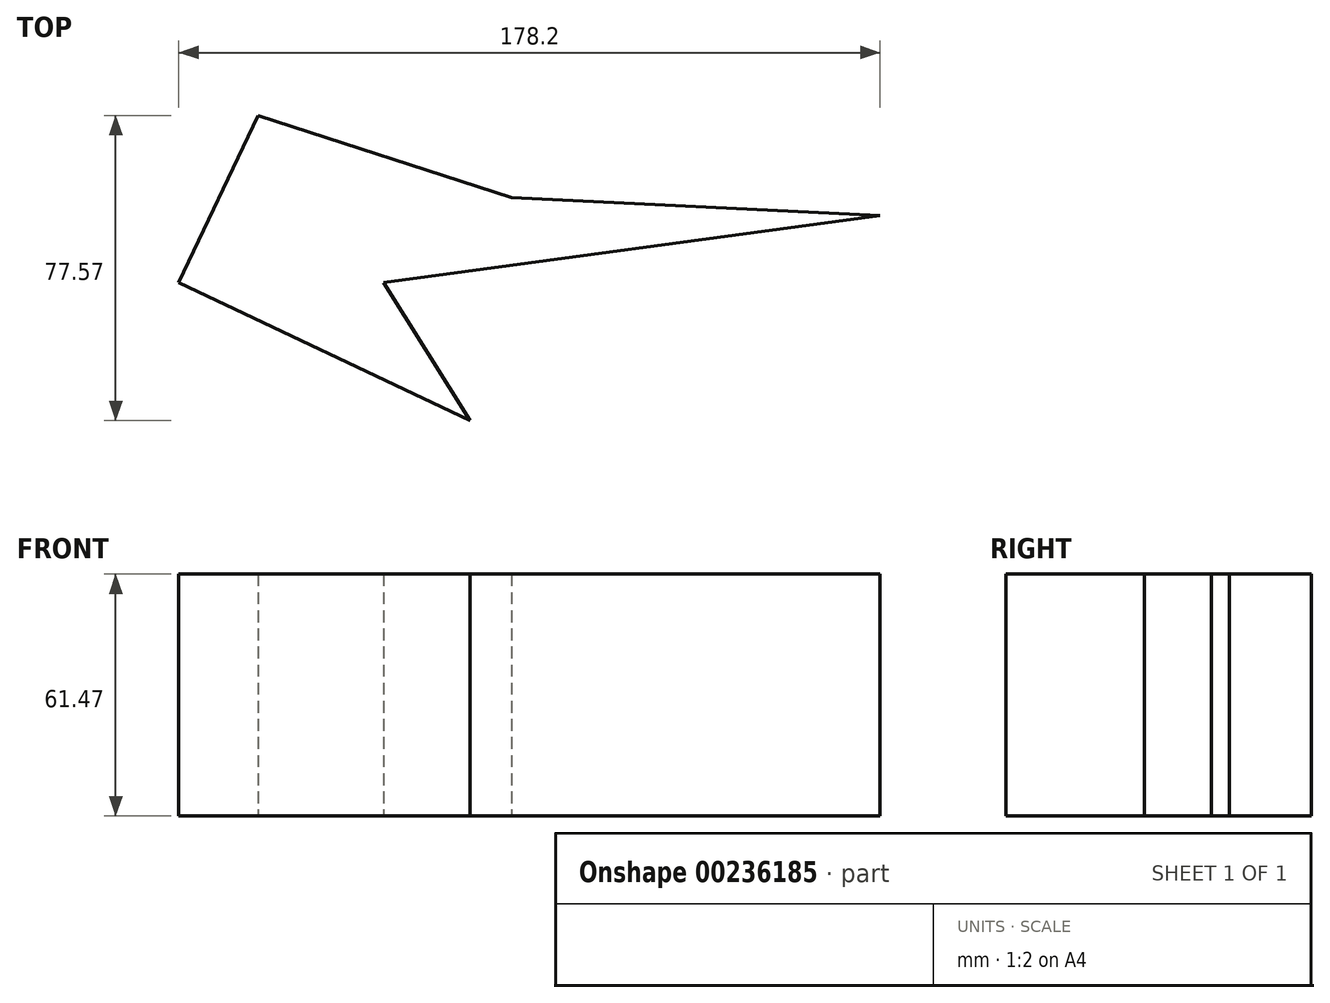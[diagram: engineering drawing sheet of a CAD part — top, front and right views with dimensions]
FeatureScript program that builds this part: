
annotation { "Feature Type Name" : "Feature", "Feature Type Description" : "" }
export const myFeature = defineFeature(function(context is Context, id is Id, definition is map)
    precondition{}
    {
        {
            var Q0;
            Q0=qCreatedBy(makeId("Top.planeOp"),FACE);
            var sketch = newSketch(context, id + "F0", { "sketchPlane" : qUnion([Q0])});
            skLineSegment(sketch, "E0", {"start": v(44.55, 16.26) * mm, "end": v(-19.8, 37.13) * mm});
            skLineSegment(sketch, "E1", {"start": v(-19.8, 37.13) * mm, "end": v(-39.95, -5.3) * mm});
            skLineSegment(sketch, "E2", {"start": v(-39.95, -5.3) * mm, "end": v(34.01, -40.44) * mm});
            skLineSegment(sketch, "E3", {"start": v(34.01, -40.44) * mm, "end": v(12.02, -5.3) * mm});
            skLineSegment(sketch, "E4", {"start": v(12.02, -5.3) * mm, "end": v(138.25, 11.67) * mm});
            skLineSegment(sketch, "E5", {"start": v(138.25, 11.67) * mm, "end": v(44.55, 16.26) * mm});
            skSolve(sketch);
        }
        {
            var Q0;
            Q0 = qSketchRegion(id + "F0", true);
            extrude(context, id + "F1", {"entities" : qUnion([Q0]), "depth" : 61.47 * mm});
        }
    });
